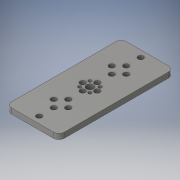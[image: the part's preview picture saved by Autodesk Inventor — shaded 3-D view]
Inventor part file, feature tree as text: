
AUTODESK INVENTOR PART (.ipt)
format: ipt  version: 2016 (Build 200138000, 138)  size: 187,392 bytes
history: native  units: mm
features: reference x19, sketch x2, extrude x1, hole x1, projected_geometry x1
ambient origin geometry x8: Origin, YZ Plane, XZ Plane, XY Plane, X Axis, Y Axis, Z Axis, Center Point
bodies: Body1 (feature_tree)
feature tree (24):
  extrude  "Extrusion2"  Depth=126.62mm
  hole  "Hole2"  [1 undecoded]
  sketch  "Sketch1"  dims[d9=6.0mm d10=0.0mm]
  reference  "Reference1"
  reference  "Reference2"
  reference  "Reference3"
  reference  "Reference4"
  reference  "Reference5"
  reference  "Reference6"
  reference  "Reference7"
  reference  "Reference8"
  reference  "Reference9"
  reference  "Reference10"
  reference  "Reference11"
  reference  "Reference12"
  reference  "Reference13"
  reference  "Reference14"
  reference  "Reference15"
  reference  "Reference16"
  reference  "Reference17"
  reference  "Reference18"
  reference  "Reference19"
  sketch  "Sketch3"  dims[d11=3.7mm d12=6.0mm d13=6.0mm d14=3.5mm d15=90.0deg d16=8.0mm d17=20.594885mm d18=126.62mm d19=58.04mm]
  projected_geometry  "Projected Loop1"
note: 1 required parameter value undecoded (feature->parameter linkage not recoverable at this tier; creation-order binding heuristic only, values carry confidence <= 0.55)
